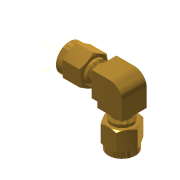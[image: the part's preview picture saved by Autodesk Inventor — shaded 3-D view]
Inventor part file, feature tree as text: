
AUTODESK INVENTOR PART (.ipt)
format: ipt  version: 2016 SP2 (Build 200236200, 236)  size: 215,040 bytes
history: native  units: mm
features: sketch x1, other x1
ambient origin geometry x8: Origin, YZ Plane, XZ Plane, XY Plane, X Axis, Y Axis, Z Axis, Center Point
bodies: Solid1 (feature_tree)
feature tree (2):
  sketch  "Sketch1"
  other  "LUMP1"
